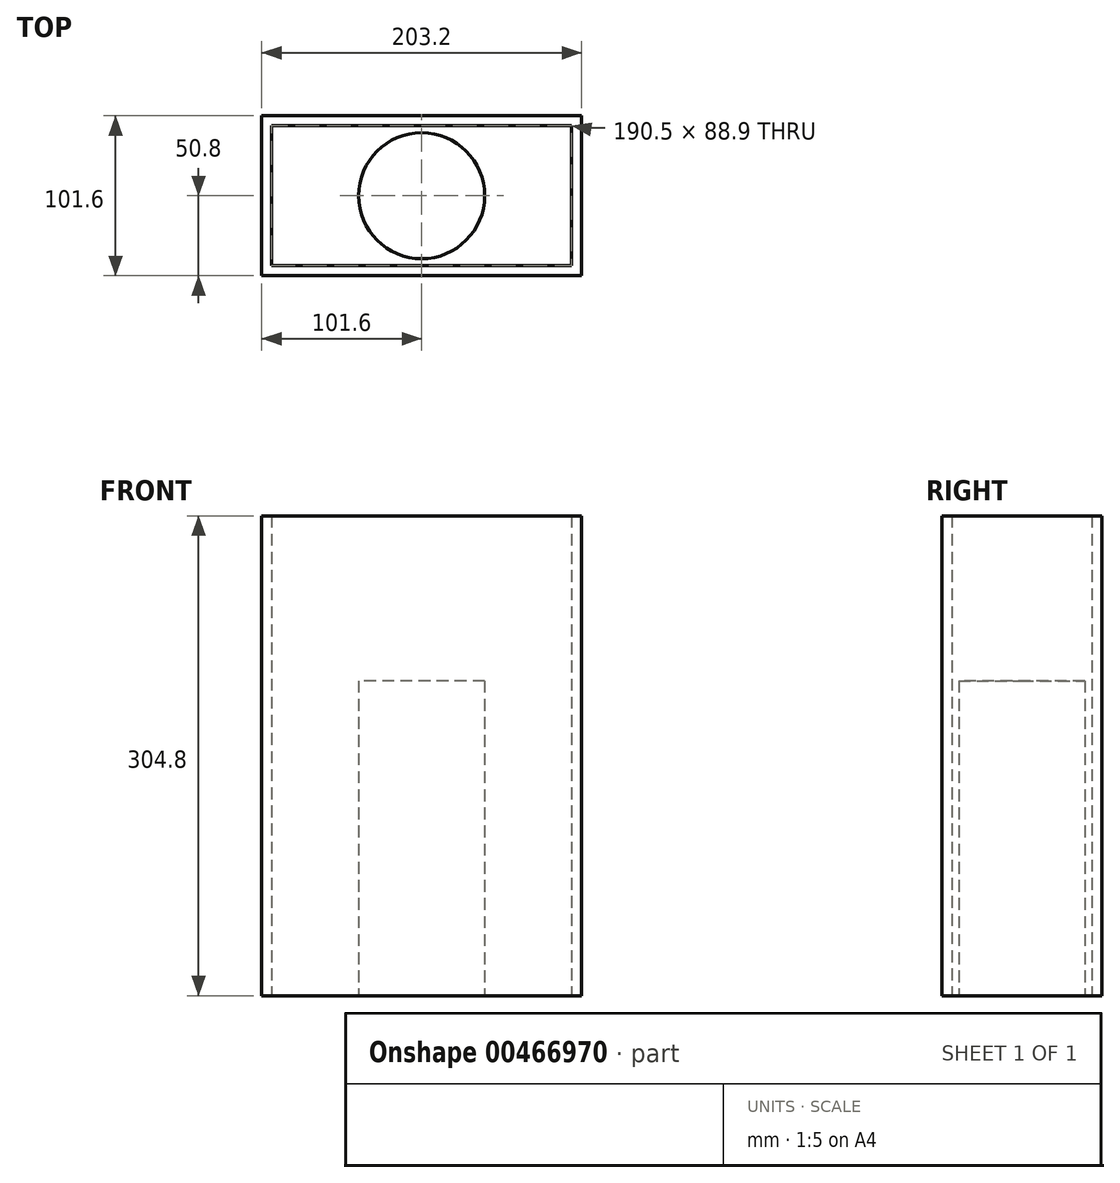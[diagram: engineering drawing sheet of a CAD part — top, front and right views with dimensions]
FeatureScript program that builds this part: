
annotation { "Feature Type Name" : "Feature", "Feature Type Description" : "" }
export const myFeature = defineFeature(function(context is Context, id is Id, definition is map)
    precondition{}
    {
        {
            var Q0;
            Q0=qCreatedBy(makeId("Top.planeOp"),FACE);
            var sketch = newSketch(context, id + "F0", { "sketchPlane" : qUnion([Q0])});
            skLineSegment(sketch, "E0.bottom", {"start": v(101.6, 50.8) * mm, "end": v(-101.6, 50.8) * mm});
            skLineSegment(sketch, "E0.top", {"start": v(101.6, -50.8) * mm, "end": v(-101.6, -50.8) * mm});
            skLineSegment(sketch, "E0.left", {"start": v(101.6, 50.8) * mm, "end": v(101.6, -50.8) * mm});
            skLineSegment(sketch, "E0.right", {"start": v(-101.6, 50.8) * mm, "end": v(-101.6, -50.8) * mm});
            skPoint(sketch, "E0.middle", {"position": v(0, 0) * mm});
            skLineSegment(sketch, "E1.0", {"start": v(-95.25, 44.45) * mm, "end": v(-95.25, -44.45) * mm});
            skLineSegment(sketch, "E1.1", {"start": v(95.25, 44.45) * mm, "end": v(-95.25, 44.45) * mm});
            skLineSegment(sketch, "E1.2", {"start": v(95.25, 44.45) * mm, "end": v(95.25, -44.45) * mm});
            skLineSegment(sketch, "E1.3", {"start": v(95.25, -44.45) * mm, "end": v(-95.25, -44.45) * mm});
            skCircle(sketch, "E2", {"center": v(0, 0) * mm, "radius": 40 * mm});
            skLineSegment(sketch, "E3.bottom", {"start": v(17, 55.6) * mm, "end": v(-17, 55.6) * mm});
            skLineSegment(sketch, "E3.top", {"start": v(17, 67.6) * mm, "end": v(-17, 67.6) * mm});
            skLineSegment(sketch, "E3.left", {"start": v(17, 55.6) * mm, "end": v(17, 67.6) * mm});
            skLineSegment(sketch, "E3.right", {"start": v(-17, 55.6) * mm, "end": v(-17, 67.6) * mm});
            skPoint(sketch, "E3.middle", {"position": v(0, 61.6) * mm});
            skLineSegment(sketch, "E4", {"start": v(0, 0) * mm, "end": v(0, -31.77) * mm, "construction": true});
            skLineSegment(sketch, "E5.bottom", {"start": v(95.25, 31.5) * mm, "end": v(65.25, 31.5) * mm, "construction": true});
            skLineSegment(sketch, "E5.top", {"start": v(95.25, -31.5) * mm, "end": v(65.25, -31.5) * mm, "construction": true});
            skLineSegment(sketch, "E5.left", {"start": v(95.25, 31.5) * mm, "end": v(95.25, -31.5) * mm, "construction": true});
            skLineSegment(sketch, "E5.right", {"start": v(65.25, 31.5) * mm, "end": v(65.25, -31.5) * mm, "construction": true});
            skPoint(sketch, "E5.middle", {"position": v(80.25, 0) * mm});
            skLineSegment(sketch, "E6.MirrorCS", {"start": v(-95.25, 31.5) * mm, "end": v(-95.25, -31.5) * mm, "construction": true});
            skLineSegment(sketch, "E7.MirrorCS", {"start": v(-95.25, 31.5) * mm, "end": v(-65.25, 31.5) * mm, "construction": true});
            skLineSegment(sketch, "E8.MirrorCS", {"start": v(-95.25, -31.5) * mm, "end": v(-65.25, -31.5) * mm, "construction": true});
            skLineSegment(sketch, "E9.MirrorCS", {"start": v(-65.25, 31.5) * mm, "end": v(-65.25, -31.5) * mm, "construction": true});
            skPoint(sketch, "E10.MirrorP", {"position": v(-80.25, 0) * mm});
            skLineSegment(sketch, "E11.bottom", {"start": v(58.29, 17) * mm, "end": v(58.29, -17) * mm, "construction": true});
            skLineSegment(sketch, "E11.top", {"start": v(46.29, 17) * mm, "end": v(46.29, -17) * mm, "construction": true});
            skLineSegment(sketch, "E11.left", {"start": v(58.29, 17) * mm, "end": v(46.29, 17) * mm, "construction": true});
            skLineSegment(sketch, "E11.right", {"start": v(58.29, -17) * mm, "end": v(46.29, -17) * mm, "construction": true});
            skPoint(sketch, "E11.middle", {"position": v(52.29, 0) * mm});
            skCircle(sketch, "E12", {"center": v(52.29, 0) * mm, "radius": 4 * mm, "construction": true});
            skSolve(sketch);
        }
        {
            var Q0;
            Q0=makeQuery(id+"F0.imprint","IMPRINT",FACE,{"disambiguationData":[TD([[makeQuery(id+"F0.imprint","IMPRINT",EDGE,{"derivedFrom":sQuery(id+"F0.wireOp",EDGE,"E0.bottom")}),1.0]])]});
            extrude(context, id + "F1", {"entities" : qUnion([Q0]), "depth" : 304.8 * mm});
        }
        {
            var Q0;
            Q0=makeQuery(id+"F0.imprint","IMPRINT",FACE,{"disambiguationData":[TD([[makeQuery(id+"F0.imprint","IMPRINT",EDGE,{"derivedFrom":sQuery(id+"F0.wireOp",EDGE,"E2")}),1.0]])]});
            extrude(context, id + "F2", {"entities" : qUnion([Q0]), "depth" : 200 * mm});
        }
    });
